# Revit family: Catfoot
name_source: partatom
category: Furniture
units: mm (PartAtom-declared; Revit-internal decimal feet)

## family parameters
Always vertical = Yes
Cut with Voids When Loaded = No
OmniClass Number = 23.21.23.13.15
Room Calculation Point = No
Shared = No
Work Plane-Based = No

## types (1)
- 8002753
    BIM Category = Litter Bins
    Body material = Plastic, Gray
    Body material_90 = Hags - Steel - Powder coated - Green
    Construction material = Hags - Steel - Galvanized
    Default Elevation = 0 mm  [stored 0 ft]
    Description = Sofa Sofiero Detached
    Edition number = 1
    IFC Classification = Furniture
    Manufacturer = Hags
    Manufacturer name = HAGS
    Model = 8037012
    OmniClass Code = 23-21 23 13 15
    OmniClass Description = Litter Bin
    Product Guid = 90e49432-c870-4a59-897e-b15016e8f9bd
    Product SKU = Catfoot_Detached
    Product data url = https://bimobject.com
    Product name = Catfoot Litter Bin
    Product url = https://hags.se
    QR code = https://www.hags.com
    URL = https://www.hags.com
    Uniclass 1.4 Code = L8211
    Uniclass 1.4 Description = Furniture

note: [stored X ft] marks values corroborated as IEEE doubles in the binary element streams (Revit-internal decimal feet)

## geometry (parser evidence)
native form markers: Sweep x2
no freeform markers — native parametric forms only
